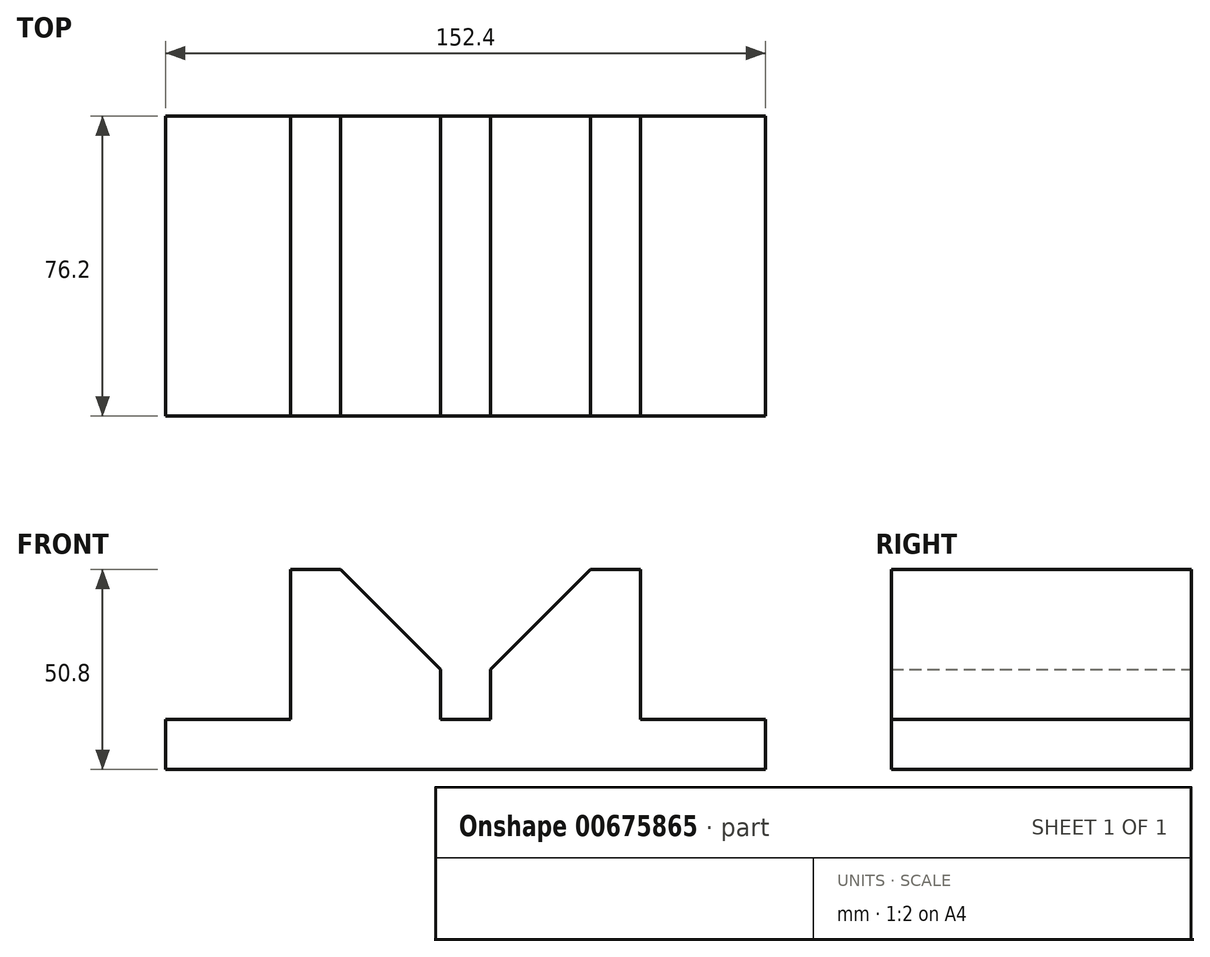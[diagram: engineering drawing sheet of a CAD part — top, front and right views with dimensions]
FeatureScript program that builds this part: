
annotation { "Feature Type Name" : "Feature", "Feature Type Description" : "" }
export const myFeature = defineFeature(function(context is Context, id is Id, definition is map)
    precondition{}
    {
        {
            var Q0;
            Q0=qCreatedBy(makeId("Front.planeOp"),FACE);
            var sketch = newSketch(context, id + "F0", { "sketchPlane" : qUnion([Q0])});
            skLineSegment(sketch, "E0", {"start": v(-63.16, 14.08) * mm, "end": v(-63.16, -24.02) * mm});
            skLineSegment(sketch, "E1", {"start": v(-63.16, -24.02) * mm, "end": v(-94.9, -24.02) * mm});
            skLineSegment(sketch, "E2", {"start": v(-94.9, -24.02) * mm, "end": v(-94.9, -36.72) * mm});
            skLineSegment(sketch, "E3", {"start": v(-94.9, -36.72) * mm, "end": v(57.5, -36.72) * mm});
            skLineSegment(sketch, "E4", {"start": v(57.5, -36.72) * mm, "end": v(57.5, -24.02) * mm});
            skLineSegment(sketch, "E5", {"start": v(57.5, -24.02) * mm, "end": v(25.74, -24.02) * mm});
            skLineSegment(sketch, "E6", {"start": v(25.74, -24.02) * mm, "end": v(25.74, 14.08) * mm});
            skLineSegment(sketch, "E7", {"start": v(-25.06, -24.02) * mm, "end": v(-12.36, -24.02) * mm});
            skLineSegment(sketch, "E8", {"start": v(-12.36, -24.02) * mm, "end": v(-12.36, -11.32) * mm});
            skLineSegment(sketch, "E9", {"start": v(-25.06, -24.02) * mm, "end": v(-25.06, -11.32) * mm});
            skLineSegment(sketch, "E10", {"start": v(-63.16, 14.08) * mm, "end": v(-50.46, 14.08) * mm});
            skPoint(sketch, "E11.start.orphan", {"position": v(0, 17.41) * mm});
            skLineSegment(sketch, "E12", {"start": v(25.74, 14.08) * mm, "end": v(13.04, 14.08) * mm});
            skLineSegment(sketch, "E13", {"start": v(-50.46, 14.08) * mm, "end": v(-25.06, -11.32) * mm});
            skLineSegment(sketch, "E14", {"start": v(13.04, 14.08) * mm, "end": v(-12.36, -11.32) * mm});
            skSolve(sketch);
        }
        {
            var Q0;
            Q0=makeQuery(id+"F0.imprint","IMPRINT",FACE,{"disambiguationData":[TD([[makeQuery(id+"F0.imprint","IMPRINT",EDGE,{"derivedFrom":sQuery(id+"F0.wireOp",EDGE,"E0")}),1.0]])]});
            extrude(context, id + "F1", {"entities" : qUnion([Q0]), "depth" : 76.2 * mm, "offsetDistance" : 25.4 * mm});
        }
    });
